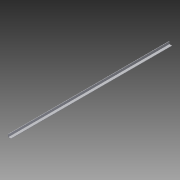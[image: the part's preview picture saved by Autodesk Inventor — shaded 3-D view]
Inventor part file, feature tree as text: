
AUTODESK INVENTOR PART (.ipt)
format: ipt  version: 2013 (Build 170138000, 138)  size: 73,728 bytes
history: native  units: in
note: dims shown in document units (in); Inventor stores cm internally (conversion verified against a paired STEP export)
features: extrude x1, sketch x1
ambient origin geometry x8: Origin, YZ Plane, XZ Plane, XY Plane, X Axis, Y Axis, Z Axis, Center Point
bodies: Solid1 (feature_tree)
feature tree (2):
  extrude  "Extrusion1"  Depth=0.0625in
  sketch  "Sketch1"  dims[d0=0.5in d1=0.0625in d2=0.5in d3=0.0625in d4=28.375in d5=0.0in]
